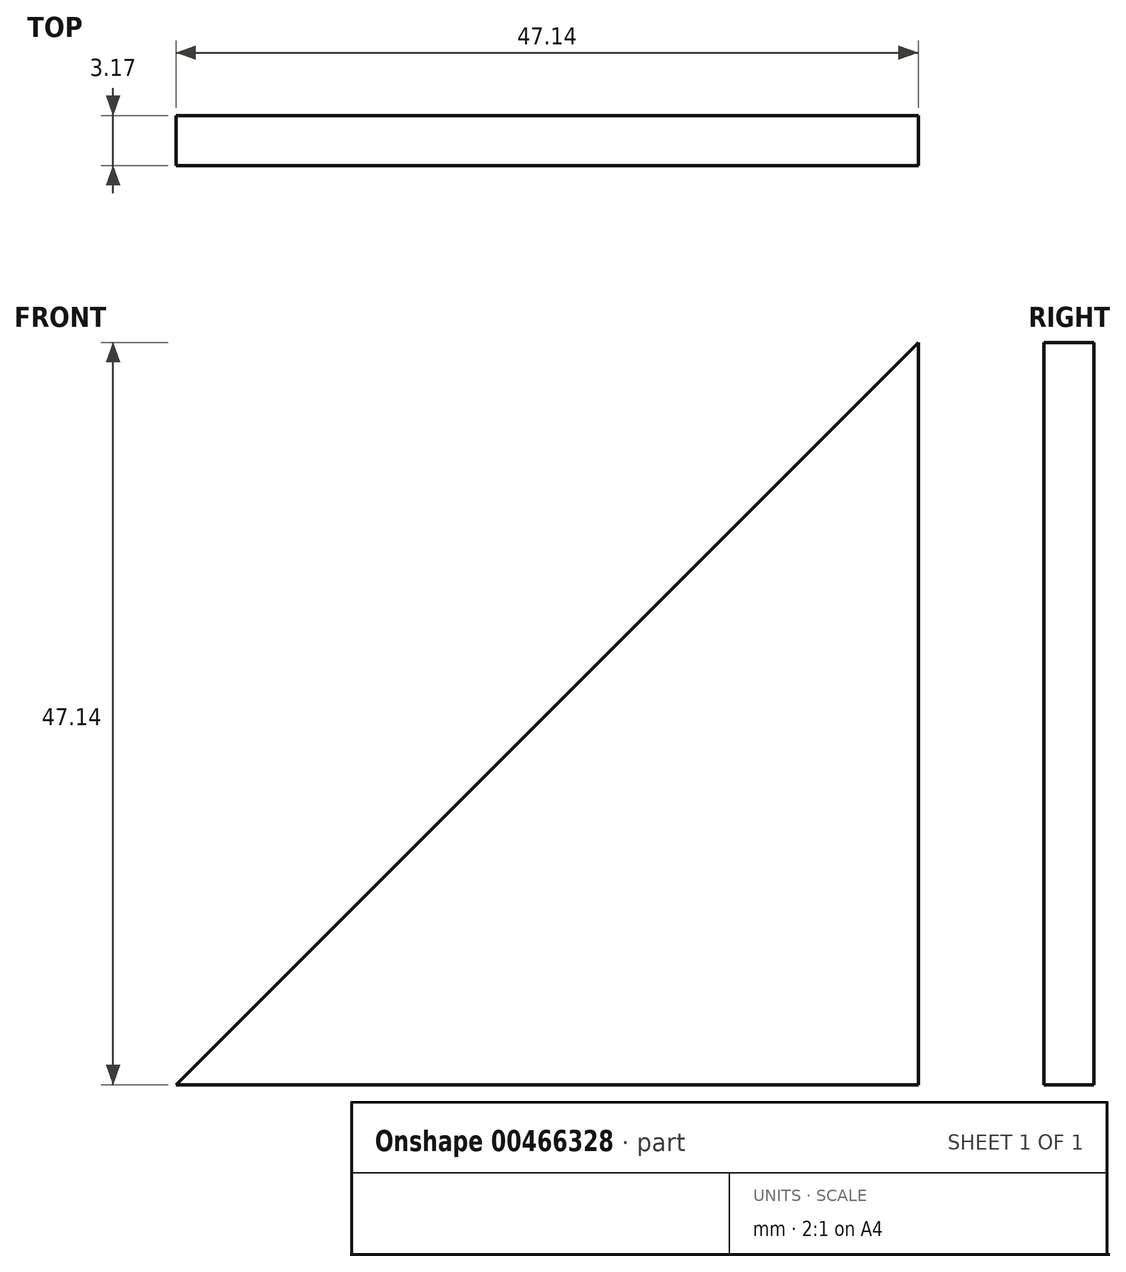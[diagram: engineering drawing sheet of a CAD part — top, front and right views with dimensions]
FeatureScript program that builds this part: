
annotation { "Feature Type Name" : "Feature", "Feature Type Description" : "" }
export const myFeature = defineFeature(function(context is Context, id is Id, definition is map)
    precondition{}
    {
        {
            var Q0;
            Q0=qCreatedBy(makeId("Front.planeOp"),FACE);
            var sketch = newSketch(context, id + "F0", { "sketchPlane" : qUnion([Q0])});
            skLineSegment(sketch, "E0", {"start": v(-40.91, 2.55) * mm, "end": v(6.23, 49.7) * mm});
            skLineSegment(sketch, "E1", {"start": v(-40.91, 2.55) * mm, "end": v(6.23, 2.55) * mm});
            skLineSegment(sketch, "E2", {"start": v(6.23, 49.7) * mm, "end": v(6.23, 2.55) * mm});
            skSolve(sketch);
        }
        {
            var Q0;
            Q0=makeQuery(id+"F0.imprint","IMPRINT",FACE,{"disambiguationData":[TD([[makeQuery(id+"F0.imprint","IMPRINT",EDGE,{"derivedFrom":sQuery(id+"F0.wireOp",EDGE,"E0")}),-1.0]])]});
            var Q1;
            Q1=makeQuery(id+"F0.imprint","IMPRINT",FACE,{"disambiguationData":[TD([[makeQuery(id+"F0.imprint","IMPRINT",EDGE,{"derivedFrom":sQuery(id+"F0.wireOp",EDGE,"E2")}),1.0]])]});
            extrude(context, id + "F1", {"entities" : qUnion([Q0, Q1]), "depth" : 3.17 * mm});
        }
    });
